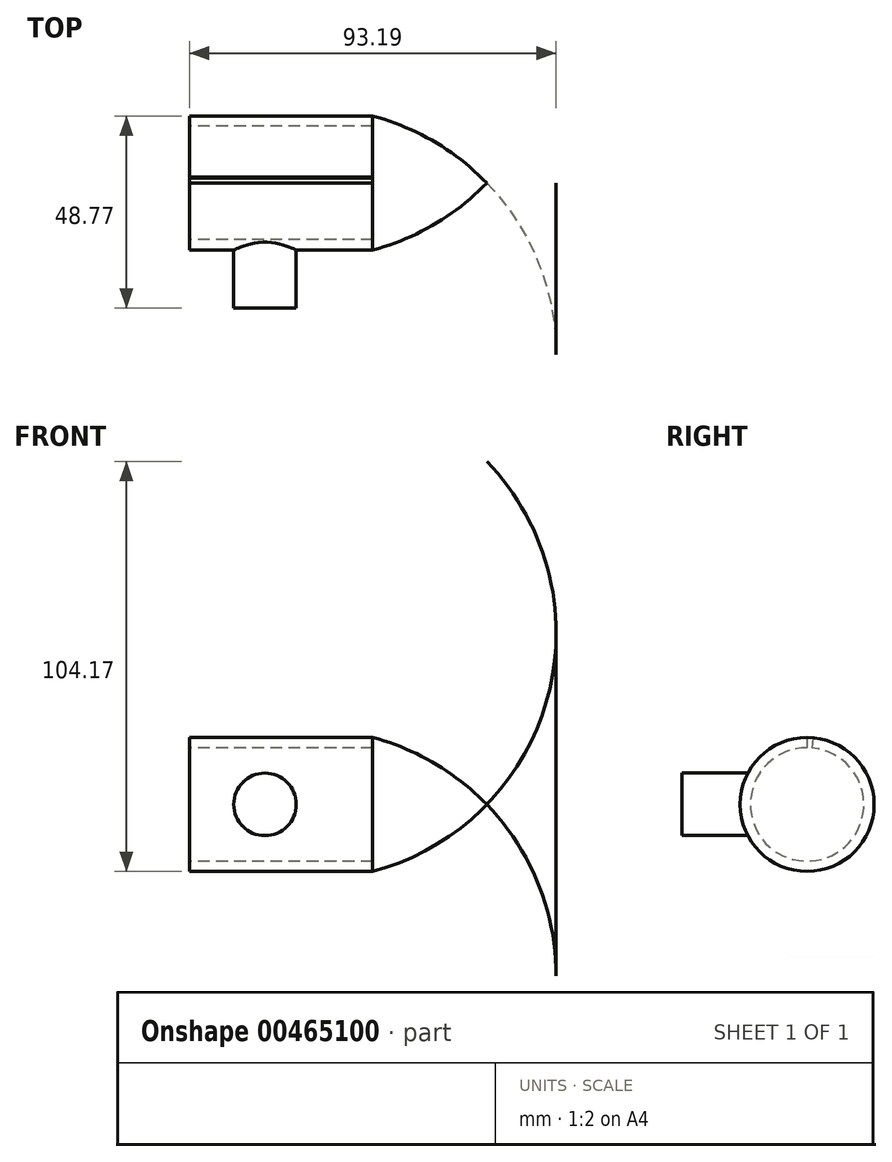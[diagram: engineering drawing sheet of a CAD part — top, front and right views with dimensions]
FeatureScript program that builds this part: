
annotation { "Feature Type Name" : "Feature", "Feature Type Description" : "" }
export const myFeature = defineFeature(function(context is Context, id is Id, definition is map)
    precondition{}
    {
        {
            var Q0;
            Q0=qCreatedBy(makeId("Front.planeOp"),FACE);
            var sketch = newSketch(context, id + "F0", { "sketchPlane" : qUnion([Q0])});
            skLineSegment(sketch, "E0.1", {"start": v(-86.62, 31.5) * mm, "end": v(-86.62, 14.48) * mm});
            skArc(sketch, "E0.3", {"start": v(-11.05, 14.48) * mm, "mid": v(-24.39, 24.97) * mm, "end": v(-40.05, 31.5) * mm});
            skLineSegment(sketch, "E0.4", {"start": v(-86.62, 31.5) * mm, "end": v(-40.05, 31.5) * mm});
            skLineSegment(sketch, "E1", {"start": v(-86.62, 14.48) * mm, "end": v(-11.05, 14.48) * mm});
            skPoint(sketch, "E2.orphan", {"position": v(-86.62, -2.54) * mm});
            skLineSegment(sketch, "E3", {"start": v(-40.05, 31.5) * mm, "end": v(-40.05, 14.48) * mm});
            skSolve(sketch);
        }
        {
            var Q0;
            {var subQ0=sQuery(id+"F0.wireOp",EDGE,"E0.1");Q0=makeQuery(id+"F0.imprint","IMPRINT",FACE,{"disambiguationData":[TD([[makeQuery(id+"F0.imprint","IMPRINT",EDGE,{"derivedFrom":subQ0}),1.0]])]});}
            var Q1;
            Q1=sQuery(id+"F0.wireOp",EDGE,"E1");
            revolve(context, id + "F1", {"entities" : qUnion([Q0]), "axis" : qUnion([Q1]), "revolveType" : RevolveType.ONE_DIRECTION, "angle" : 355 * degree});
        }
        {
            var Q0;
            Q0=makeQuery(id+"F1.opRevolve","SWEPT_FACE",FACE,{"disambiguationData":[OSD([sQuery(id+"F0.wireOp",EDGE,"E0.1")])]});
            var sketch = newSketch(context, id + "F2", { "sketchPlane" : qUnion([Q0])});
            skPoint(sketch, "E4", {"position": v(0, 14.48) * mm});
            skSolve(sketch);
        }
        {
            var Q0;
            Q0=sQuery(id+"F2.wireOp",VERTEX,"E4");
            var Q1;
            Q1=makeQuery(id+"F1.opRevolve","SWEPT_BODY",BODY,{"disambiguationData":[OSD([sQuery(id+"F0.wireOp",EDGE,"E0.1"),sQuery(id+"F0.wireOp",EDGE,"E0.3"),sQuery(id+"F0.wireOp",EDGE,"E0.4"),sQuery(id+"F0.wireOp",EDGE,"E1")])]});
            hole(context, id + "F3", {"style" : HoleStyle.SIMPLE, "endStyle" : HoleEndStyle.BLIND, "holeDiameter" : 28.83 * mm, "holeDepth" : 50.8 * mm, "isTappedThrough" : true, "tappedDepth" : 12.7 * mm, "tapClearance" : 3, "startFromSketch" : true, "locations" : qUnion([Q0]), "scope" : qUnion([Q1])});
        }
        {
            var Q0;
            {var subQ0=sQuery(id+"F0.wireOp",EDGE,"E0.3");Q0=makeQuery(id+"F0.imprint","IMPRINT",FACE,{"disambiguationData":[TD([[makeQuery(id+"F0.imprint","IMPRINT",EDGE,{"derivedFrom":subQ0}),1.0]])]});}
            var Q1;
            Q1=sQuery(id+"F0.wireOp",EDGE,"E1");
            revolve(context, id + "F4", {"entities" : qUnion([Q0]), "axis" : qUnion([Q1]), "revolveType" : RevolveType.FULL});
        }
        {
            var Q0;
            Q0=qCreatedBy(makeId("Front.planeOp"),FACE);
            cPlane(context, id + "F5", {"entities" : qUnion([Q0]), "cplaneType" : CPlaneType.OFFSET, "offset" : 25.4 * mm, "width" : 152.4 * mm, "height" : 152.4 * mm});
        }
        {
            var Q0;
            Q0=qCreatedBy(id+"F5.planeOp",FACE);
            var sketch = newSketch(context, id + "F6", { "sketchPlane" : qUnion([Q0])});
            skCircle(sketch, "E5", {"center": v(-67.41, 14.51) * mm, "radius": 7.94 * mm});
            skLineSegment(sketch, "E6", {"start": v(-67.41, 14.51) * mm, "end": v(-59.47, 14.51) * mm});
            skLineSegment(sketch, "E7", {"start": v(-67.41, 14.51) * mm, "end": v(-67.41, 22.45) * mm});
            skSolve(sketch);
        }
        {
            var Q0;
            Q0 = qSketchRegion(id + "F6", true);
            extrude(context, id + "F7", {"entities" : qUnion([Q0]), "operationType" : NewBodyOperationType.ADD, "endBound" : BoundingType.UP_TO_NEXT, "oppositeDirection" : true, "depth" : 25.4 * mm});
        }
        {
            var Q0;
            Q0=makeQuery(id+"F7.opExtrude","CAP_FACE",FACE,{"disambiguationData":[OSD([sQuery(id+"F6.wireOp",EDGE,"E5")])],"isStart":true});
            var sketch = newSketch(context, id + "F8", { "sketchPlane" : qUnion([Q0])});
            skPoint(sketch, "E8", {"position": v(-67.41, 14.51) * mm});
            skSolve(sketch);
        }
        {
            var Q0;
            Q0=makeQuery(id+"F8.imprint","IMPRINT",FACE,{"disambiguationData":[TD([[makeQuery(id+"F8.imprint","IMPRINT",EDGE,{"derivedFrom":makeQuery(id+"F7.opExtrude","CAP_EDGE",EDGE,{"disambiguationData":[OSD([sQuery(id+"F6.wireOp",EDGE,"E5")])],"isStart":true})}),1.0]])]});
            extrude(context, id + "F9", {"entities" : qUnion([Q0]), "operationType" : NewBodyOperationType.ADD, "depth" : 6.35 * mm});
        }
    });
